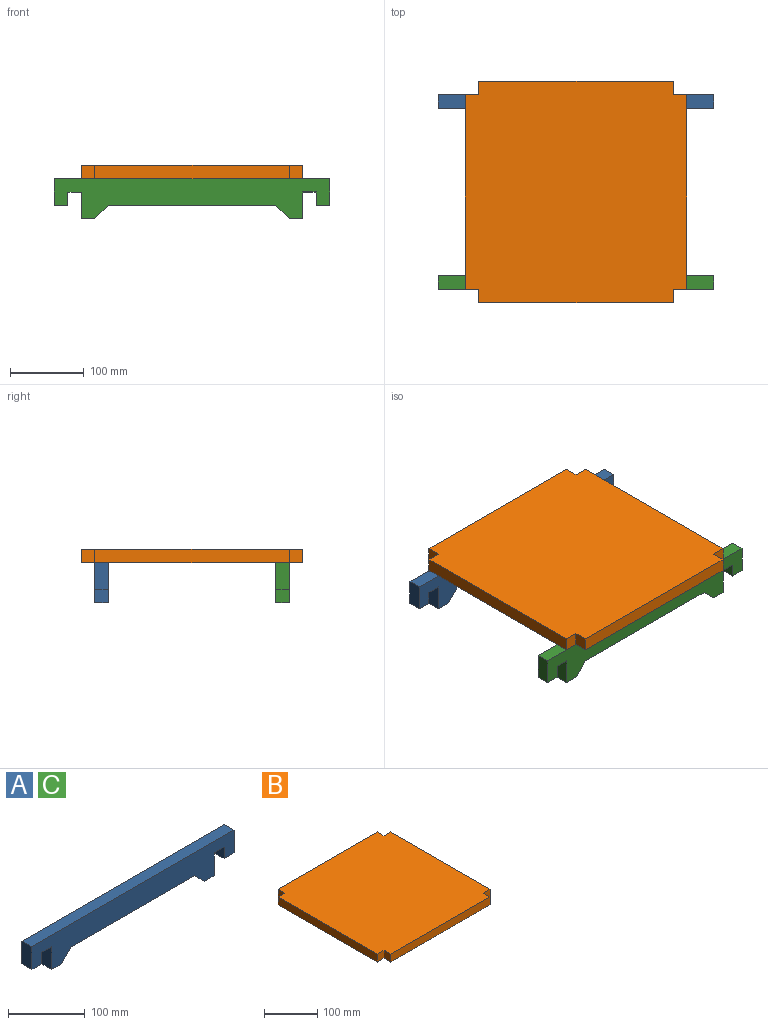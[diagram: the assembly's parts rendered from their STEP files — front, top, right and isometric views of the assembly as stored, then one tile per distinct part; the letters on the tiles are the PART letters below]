
ASSEMBLY  parts=3 mates=2
PART A: 18 faces, bbox 372.8x18.2x54.6 mm
  f0: plane 36.4x18.2mm, normal (1,0,0), area 662.5mm2, adj f1,f15,f16,f17
  f1: plane 372.8x18.2mm, normal (0,0,1), area 6785mm2, adj f0,f2,f16,f17
  f2: plane 36.4x18.2mm, normal (-1,0,0), area 662.5mm2, adj f1,f3,f16,f17
  f3: plane 18.2x18.2mm, normal (0,0,-1), area 331.2mm2, adj f2,f4,f16,f17
  f4: plane 18.2x18.2mm, normal (1,0,0), area 331.2mm2, adj f3,f5,f16,f17
  f5: plane 18.2x18.2mm, normal (0,0,-1), area 331.2mm2, adj f4,f6,f16,f17
  f6: plane 36.4x18.2mm, normal (-1,0,0), area 662.5mm2, adj f5,f7,f16,f17
  f7: plane 18.2x18.2mm, normal (0,0,-1), area 331.2mm2, adj f6,f8,f16,f17
  f8: plane 18.2x18.2mm, normal (0.71,0,-0.71), area 468.4mm2, adj f7,f9,f16,f17
  f9: plane 227.2x18.2mm, normal (0,0,-1), area 4135mm2, adj f8,f10,f16,f17
  f10: plane 18.2x18.2mm, normal (-0.71,0,-0.71), area 468.4mm2, adj f9,f11,f16,f17
  f11: plane 18.2x18.2mm, normal (0,0,-1), area 331.2mm2, adj f10,f12,f16,f17
  f12: plane 36.4x18.2mm, normal (1,0,0), area 662.5mm2, adj f11,f13,f16,f17
  f13: plane 18.2x18.2mm, normal (0,0,-1), area 331.2mm2, adj f12,f14,f16,f17
  f14: plane 18.2x18.2mm, normal (-1,0,0), area 331.2mm2, adj f13,f15,f16,f17
  f15: plane 18.2x18.2mm, normal (0,0,-1), area 331.2mm2, adj f0,f14,f16,f17
  f16: plane 372.8x54.6mm, normal (0,-1,0), area 13901.2mm2, adj f0,f1,f2,f3,f4,f5,f6,f7
  f17: plane 372.8x54.6mm, normal (0,1,0), area 13901.2mm2, adj f0,f1,f2,f3,f4,f5,f6,f7
PART B: 14 faces, bbox 300x300x18.2 mm
  f0: plane 18.2x18.2mm, normal (1,0,0), area 331.2mm2, adj f1,f11,f12,f13
  f1: plane 18.2x18.2mm, normal (0,-1,0), area 331.2mm2, adj f0,f2,f12,f13
  f2: plane 263.6x18.2mm, normal (1,0,0), area 4797.5mm2, adj f1,f3,f12,f13
  f3: plane 18.2x18.2mm, normal (0,1,0), area 331.2mm2, adj f2,f4,f12,f13
  f4: plane 18.2x18.2mm, normal (1,0,0), area 331.2mm2, adj f3,f5,f12,f13
  f5: plane 263.6x18.2mm, normal (0,1,0), area 4797.5mm2, adj f4,f6,f12,f13
  f6: plane 18.2x18.2mm, normal (-1,0,0), area 331.2mm2, adj f5,f7,f12,f13
  f7: plane 18.2x18.2mm, normal (0,1,0), area 331.2mm2, adj f6,f8,f12,f13
  f8: plane 263.6x18.2mm, normal (-1,0,0), area 4797.5mm2, adj f7,f9,f12,f13
  f9: plane 18.2x18.2mm, normal (0,-1,0), area 331.2mm2, adj f8,f10,f12,f13
  f10: plane 18.2x18.2mm, normal (-1,0,0), area 331.2mm2, adj f9,f11,f12,f13
  f11: plane 263.6x18.2mm, normal (0,-1,0), area 4797.5mm2, adj f0,f10,f12,f13
  f12: plane 300x300mm, normal (0,0,1), area 88675mm2, adj f0,f1,f2,f3,f4,f5,f6,f7
  f13: plane 300x300mm, normal (0,0,-1), area 88675mm2, adj f0,f1,f2,f3,f4,f5,f6,f7
PART C: same geometry as A
PLACE A rot(axis=(0,0,1),180deg) t=(0,113.6,-18.2)mm
PLACE B at identity fixed
PLACE C t=(0,-113.6,-18.2)mm
MATE fastened C.f16 <-> B.f9  axis (0,-1,0) through (-150,-131.8,0)mm
MATE fastened A.f16 <-> B.f3  axis (0,1,0) through (150,131.8,0)mm
